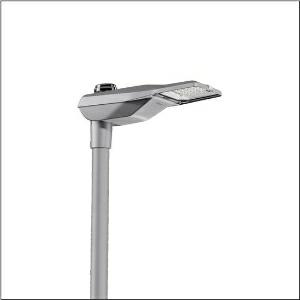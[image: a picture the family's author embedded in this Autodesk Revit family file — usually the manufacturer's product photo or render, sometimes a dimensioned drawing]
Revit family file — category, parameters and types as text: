
# Revit family: streetlight_sl_21_micro___p0_8a_5xe5u47n08cb_fda4
name_source: partatom
category: Lighting Fixtures
units: mm (PartAtom-declared; Revit-internal decimal feet)

## family parameters
Cut with Voids When Loaded = No
Host = Face
Light Source = No
Part Type = Normal
Room Calculation Point = No
Round Connector Dimension = Use Diameter
Shared = No

## types (1)
- --- (1 x LED, 2340 lm, 15.8 W, 4000K)
    Apparent Load = 16 VA
    CIE Flux Codes = 33 69 96 100 100
    Color Rendering = 70
    Color Temperature = 4000K
    Default Elevation = 1800 mm
    Description = Streetlight SL 21 micro, mast luminaire, primary light control with lens, of PMMA, primary optical cover: cover, of toughened safety glass, transparent, light distribution: P0.8a, light emission: direct distribution, primary light characteristic: asymmetric, installation type: post-top, LED, 3G 1.5mm², High Power LED, rated luminous flux: 2.340lm, luminous efficacy: 148lm/W, light colour: 740, colour temperature: 4000K, control gear: NEMA (7pin), control: flexible luminous flux parameterisation, time-dependent luminous flux control, constant luminous flux control, pre-setting: linear dimming characteristic, overheat protection, mains connection: 230..240V, AC, 50/60Hz, connection cable pre-assembled, cable length: 6,5m, wiring characteristics: H07RN-F, start of lifetime: 16W, end of service life: 16W, reduction: 8W, luminaire housing, of diecast aluminium (EN AC-44300), powder-coated, Siteco® metallic grey (DB 702S), corrosivity category C5 mid according to DIN EN ISO 12944, multi-level sealing system, sealing non-destructively replaceable, inclination adjustable: 0°, 5°, 10°, 15°, length: 528mm, width: 235mm, height: 110mm, spigot size: 76/60mm (post-top), mounting height: 4..8m, protection rating (complete): IP66, insulation class (complete): insulation class I (protective earthing), certification: CE, ENEC, ENEC+, VDE, impact resistance: IK10, permissible operating ambient temperature for outdoor applications: -40..+50°C, standard-compliant lighting for roads and squares, packaging unit: 1 piece

Light Distribution: P0.8a
    Height = 110 mm
    Lamp = 1 x LED
    Lamp Light Flux = 2340 lm
    Lamp Power = 15.8 W
    Lamp count = 1
    Length = 528 mm
    Luminous efficacy = 148 lm/W
    Manufacturer = Siteco
    ModVariant = No
    Model = 5XE5U47N08CB
    Number of Poles = 1
    OnlyDefault = Yes
    Power Factor = 1
    Product Name = Streetlight SL 21 micro | P0.8a
    Product group = mast luminaire | pylon top
    ProductGroupID = 6100
    Protection Class = Protection class I
    Protection Degree = IP 66
    RLX_Detail_Level = 1
    RLX_Emergency_Light_Flux = 0 lm
    RLX_Emergency_Type = 0
    RLX_Emergency_Type_DB = No
    RlxData = <blob elided: 98897 chars, md5=43104e05>
    Socket = socket
    Standby Power = 0 W
    System Light Flux = 2340 lm
    System Power = 16 W
    Type Comments = factory setting: luminous flux: 100 % | dim-lin: 254 | 300 mA
    Type Image = l_1294375.jpg
    URL = http://relux.com
    VarID = @adj_073806
    Voltage = 0 V
    Weight = 0.00 kg
    Width = 235 mm

## geometry (parser evidence)
native form markers: Blend x4, Sweep x10
no freeform markers — native parametric forms only
